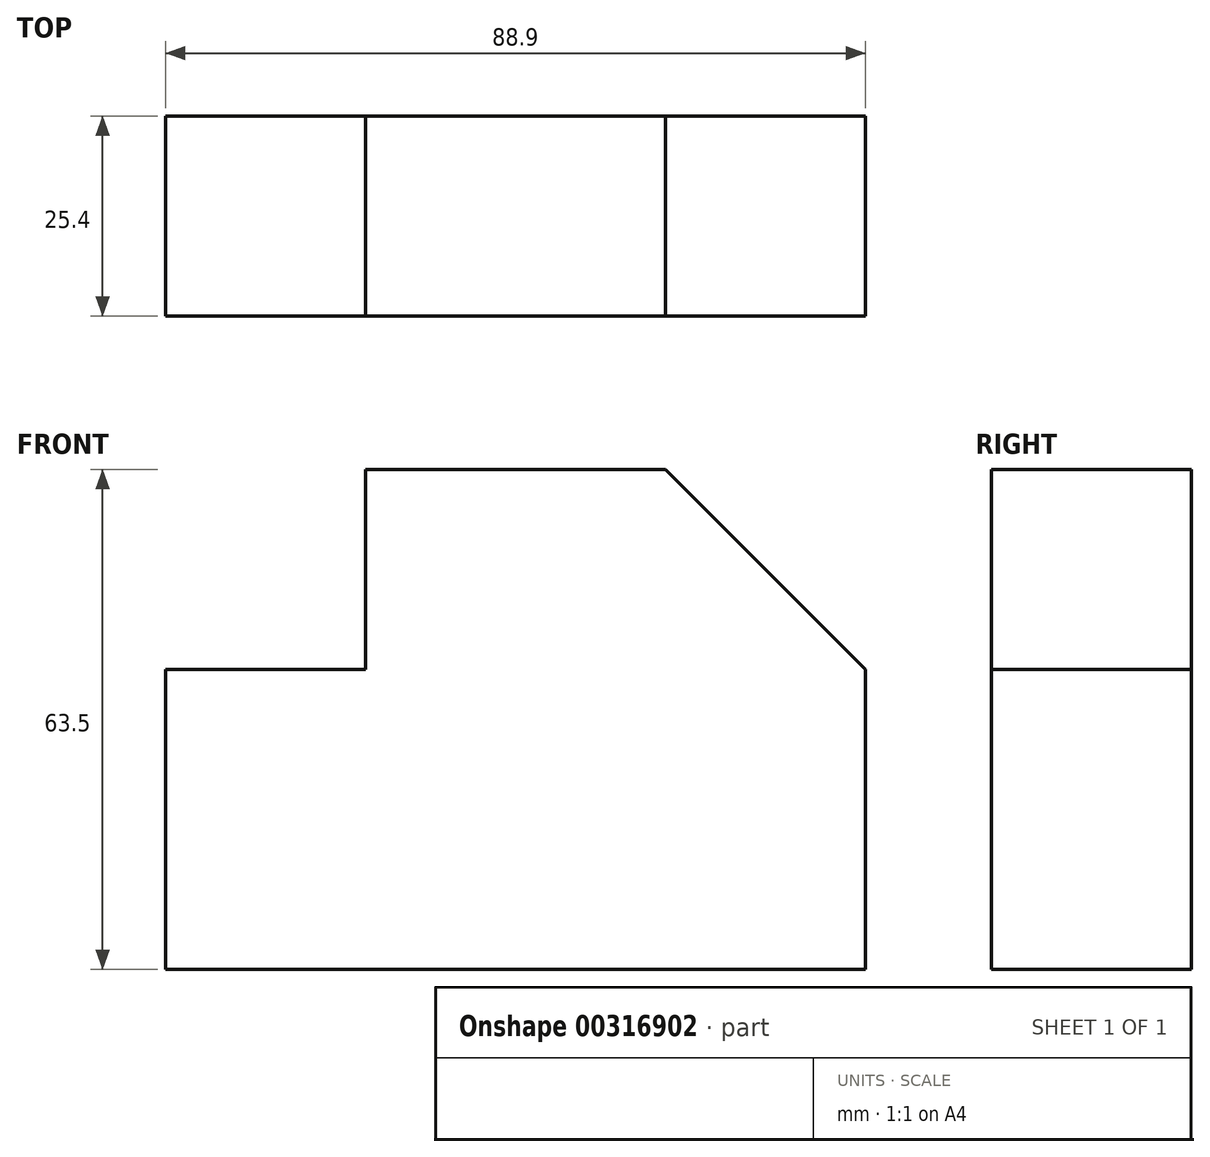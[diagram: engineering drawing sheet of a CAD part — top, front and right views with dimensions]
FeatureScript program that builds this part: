
annotation { "Feature Type Name" : "Feature", "Feature Type Description" : "" }
export const myFeature = defineFeature(function(context is Context, id is Id, definition is map)
    precondition{}
    {
        {
            var Q0;
            Q0=qCreatedBy(makeId("Front.planeOp"),FACE);
            var sketch = newSketch(context, id + "F0", { "sketchPlane" : qUnion([Q0])});
            skLineSegment(sketch, "E0", {"start": v(-70.44, -26.6) * mm, "end": v(-70.44, 11.5) * mm});
            skLineSegment(sketch, "E1", {"start": v(-70.44, 11.5) * mm, "end": v(-45.04, 11.5) * mm});
            skLineSegment(sketch, "E2", {"start": v(-45.04, 11.5) * mm, "end": v(-45.04, 36.9) * mm});
            skLineSegment(sketch, "E3", {"start": v(-45.04, 36.9) * mm, "end": v(-6.94, 36.9) * mm});
            skLineSegment(sketch, "E4", {"start": v(-6.94, 36.9) * mm, "end": v(18.46, 11.5) * mm});
            skLineSegment(sketch, "E5", {"start": v(18.46, 11.5) * mm, "end": v(18.46, -26.6) * mm});
            skLineSegment(sketch, "E6", {"start": v(18.46, -26.6) * mm, "end": v(-70.44, -26.6) * mm});
            skSolve(sketch);
        }
        {
            var Q0;
            Q0=makeQuery(id+"F0.imprint","IMPRINT",FACE,{"disambiguationData":[TD([[makeQuery(id+"F0.imprint","IMPRINT",EDGE,{"derivedFrom":sQuery(id+"F0.wireOp",EDGE,"E0")}),-1.0]])]});
            extrude(context, id + "F1", {"entities" : qUnion([Q0]), "depth" : 25.4 * mm});
        }
    });
